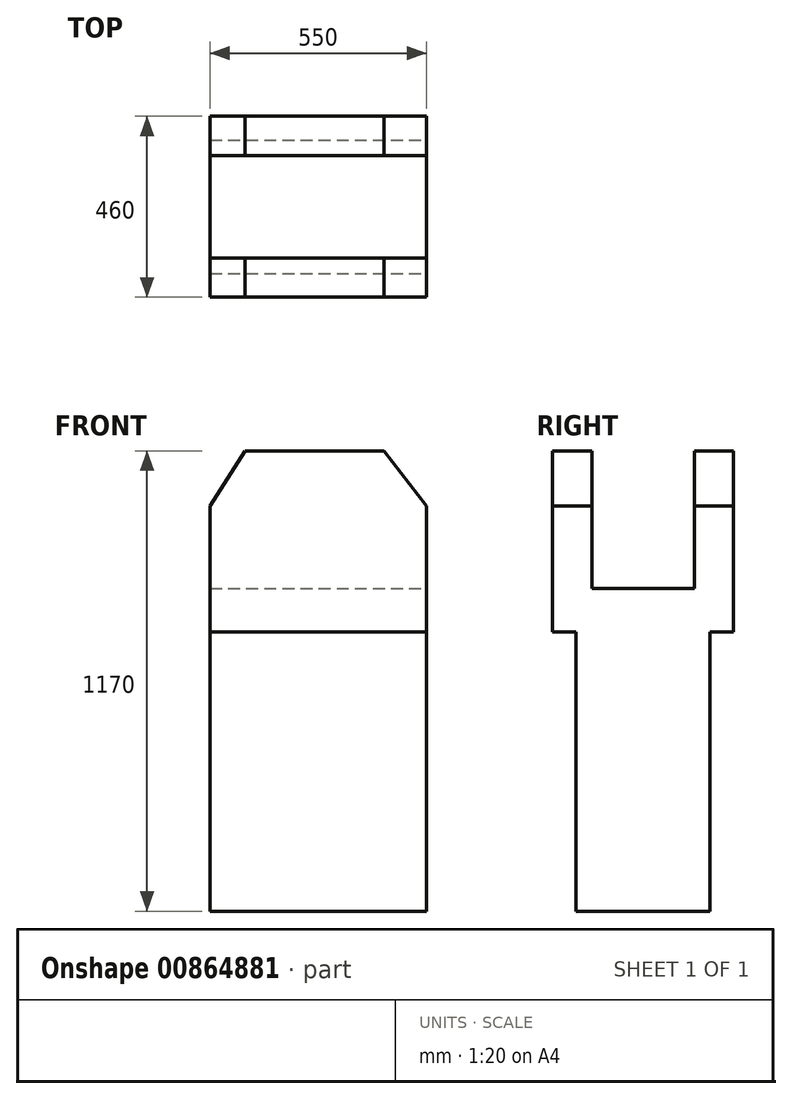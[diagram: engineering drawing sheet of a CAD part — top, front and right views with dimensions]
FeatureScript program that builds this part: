
annotation { "Feature Type Name" : "Feature", "Feature Type Description" : "" }
export const myFeature = defineFeature(function(context is Context, id is Id, definition is map)
    precondition{}
    {
        {
            var Q0;
            Q0=qCreatedBy(makeId("Right.planeOp"),FACE);
            var sketch = newSketch(context, id + "F0", { "sketchPlane" : qUnion([Q0])});
            skLineSegment(sketch, "E0.bottom", {"start": v(-230, -585) * mm, "end": v(230, -585) * mm});
            skLineSegment(sketch, "E0.top", {"start": v(-230, 585) * mm, "end": v(230, 585) * mm});
            skLineSegment(sketch, "E0.left", {"start": v(-230, -585) * mm, "end": v(-230, 585) * mm});
            skLineSegment(sketch, "E0.right", {"start": v(230, -585) * mm, "end": v(230, 585) * mm});
            skPoint(sketch, "E0.middle", {"position": v(0, 0) * mm});
            skLineSegment(sketch, "E1", {"start": v(230, 125) * mm, "end": v(156.67, 125) * mm});
            skSolve(sketch);
        }
        {
            var Q0;
            Q0 = qSketchRegion(id + "F0", true);
            extrude(context, id + "F1", {"entities" : qUnion([Q0]), "depth" : 550 * mm, "offsetDistance" : 25 * mm});
        }
        {
            var Q0;
            Q0=makeQuery(id+"F1.opExtrude","CAP_FACE",FACE,{"disambiguationData":[OSD([sQuery(id+"F0.wireOp",EDGE,"E0.bottom"),sQuery(id+"F0.wireOp",EDGE,"E0.top"),sQuery(id+"F0.wireOp",EDGE,"E0.left"),sQuery(id+"F0.wireOp",EDGE,"E0.right")])],"isStart":false});
            var sketch = newSketch(context, id + "F2", { "sketchPlane" : qUnion([Q0])});
            skLineSegment(sketch, "E2.bottom", {"start": v(-230, 125) * mm, "end": v(-170, 125) * mm});
            skLineSegment(sketch, "E2.top", {"start": v(-230, -585) * mm, "end": v(-170, -585) * mm});
            skLineSegment(sketch, "E2.left", {"start": v(-230, 125) * mm, "end": v(-230, -585) * mm});
            skLineSegment(sketch, "E2.right", {"start": v(-170, 125) * mm, "end": v(-170, -585) * mm});
            skSolve(sketch);
        }
        {
            var Q0;
            Q0 = qSketchRegion(id + "F2", true);
            extrude(context, id + "F3", {"entities" : qUnion([Q0]), "operationType" : NewBodyOperationType.REMOVE, "endBound" : BoundingType.THROUGH_ALL, "oppositeDirection" : true, "depth" : 25 * mm, "offsetDistance" : 25 * mm});
        }
        {
            var Q0;
            Q0=makeQuery(id+"F1.opExtrude","CAP_FACE",FACE,{"disambiguationData":[OSD([sQuery(id+"F0.wireOp",EDGE,"E0.bottom"),sQuery(id+"F0.wireOp",EDGE,"E0.top"),sQuery(id+"F0.wireOp",EDGE,"E0.left"),sQuery(id+"F0.wireOp",EDGE,"E0.right")])],"isStart":false});
            var sketch = newSketch(context, id + "F4", { "sketchPlane" : qUnion([Q0])});
            skLineSegment(sketch, "E3.bottom", {"start": v(230, 125) * mm, "end": v(170, 125) * mm});
            skLineSegment(sketch, "E3.top", {"start": v(230, -585) * mm, "end": v(170, -585) * mm});
            skLineSegment(sketch, "E3.left", {"start": v(230, 125) * mm, "end": v(230, -585) * mm});
            skLineSegment(sketch, "E3.right", {"start": v(170, 125) * mm, "end": v(170, -585) * mm});
            skSolve(sketch);
        }
        {
            var Q0;
            Q0 = qSketchRegion(id + "F4", true);
            extrude(context, id + "F5", {"entities" : qUnion([Q0]), "operationType" : NewBodyOperationType.REMOVE, "endBound" : BoundingType.THROUGH_ALL, "oppositeDirection" : true, "depth" : 25 * mm, "offsetDistance" : 25 * mm});
        }
        {
            var Q0;
            Q0=makeQuery(id+"F1.opExtrude","CAP_FACE",FACE,{"disambiguationData":[OSD([sQuery(id+"F0.wireOp",EDGE,"E0.bottom"),sQuery(id+"F0.wireOp",EDGE,"E0.top"),sQuery(id+"F0.wireOp",EDGE,"E0.left"),sQuery(id+"F0.wireOp",EDGE,"E0.right")])],"isStart":false});
            var sketch = newSketch(context, id + "F6", { "sketchPlane" : qUnion([Q0])});
            skLineSegment(sketch, "E4.bottom", {"start": v(-130, 235) * mm, "end": v(130, 235) * mm});
            skLineSegment(sketch, "E4.top", {"start": v(-130, 935) * mm, "end": v(130, 935) * mm});
            skLineSegment(sketch, "E4.left", {"start": v(-130, 235) * mm, "end": v(-130, 935) * mm});
            skLineSegment(sketch, "E4.right", {"start": v(130, 235) * mm, "end": v(130, 935) * mm});
            skPoint(sketch, "E4.middle", {"position": v(0, 585) * mm});
            skSolve(sketch);
        }
        {
            var Q0;
            Q0 = qSketchRegion(id + "F6", true);
            extrude(context, id + "F7", {"entities" : qUnion([Q0]), "operationType" : NewBodyOperationType.REMOVE, "endBound" : BoundingType.THROUGH_ALL, "oppositeDirection" : true, "depth" : 25 * mm, "offsetDistance" : 25 * mm});
        }
        {
            var Q0;
            Q0=makeQuery(id+"F1.opExtrude","SWEPT_FACE",FACE,{"disambiguationData":[OSD([sQuery(id+"F0.wireOp",EDGE,"E0.left")])]});
            var sketch = newSketch(context, id + "F8", { "sketchPlane" : qUnion([Q0])});
            skLineSegment(sketch, "E5", {"start": v(89.05, 585) * mm, "end": v(0, 445) * mm});
            skSolve(sketch);
        }
        {
            var Q0;
            Q0 = qSketchRegion(id + "F8", true);
            var Q1;
            {var subQ0=sQuery(id+"F8.wireOp",EDGE,"E5");Q1=makeQuery(id+"F8.imprint","IMPRINT",FACE,{"disambiguationData":[TD([[makeQuery(id+"F8.imprint","IMPRINT",EDGE,{"derivedFrom":subQ0}),-1.0]])]});}
            extrude(context, id + "F9", {"entities" : qUnion([Q0, Q1]), "operationType" : NewBodyOperationType.REMOVE, "endBound" : BoundingType.THROUGH_ALL, "oppositeDirection" : true, "depth" : 25 * mm, "offsetDistance" : 25 * mm});
        }
        {
            var Q0;
            Q0=makeQuery(id+"F1.opExtrude","SWEPT_FACE",FACE,{"disambiguationData":[OSD([sQuery(id+"F0.wireOp",EDGE,"E0.left")])]});
            var sketch = newSketch(context, id + "F10", { "sketchPlane" : qUnion([Q0])});
            skLineSegment(sketch, "E6", {"start": v(441.46, 585) * mm, "end": v(550, 445) * mm});
            skSolve(sketch);
        }
        {
            var Q0;
            Q0 = qSketchRegion(id + "F10", true);
            var Q1;
            {var subQ0=sQuery(id+"F10.wireOp",EDGE,"E6");Q1=makeQuery(id+"F10.imprint","IMPRINT",FACE,{"disambiguationData":[TD([[makeQuery(id+"F10.imprint","IMPRINT",EDGE,{"derivedFrom":subQ0}),1.0]])]});}
            extrude(context, id + "F11", {"entities" : qUnion([Q0, Q1]), "operationType" : NewBodyOperationType.REMOVE, "endBound" : BoundingType.THROUGH_ALL, "oppositeDirection" : true, "depth" : 25 * mm, "offsetDistance" : 25 * mm});
        }
    });
